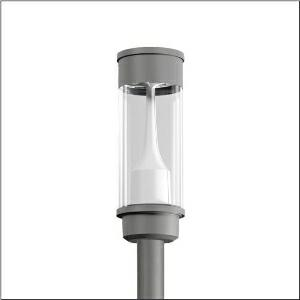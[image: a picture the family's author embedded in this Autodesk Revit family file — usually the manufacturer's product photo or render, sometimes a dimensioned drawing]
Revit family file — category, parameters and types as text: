
# Revit family: litepole_iq___p1_0a_5xa5415lf14h_d8b4
name_source: partatom
category: Lighting Fixtures
units: mm (PartAtom-declared; Revit-internal decimal feet)

## family parameters
Cut with Voids When Loaded = No
Host = Face
Light Source = No
Part Type = Normal
Room Calculation Point = No
Round Connector Dimension = Use Diameter
Shared = No

## types (1)
- --- (1 x LED, 1510 lm, 10 W, 4000K)
    Apparent Load = 10 VA
    CIE Flux Codes = 32 61 90 93 100
    Color Rendering = 70
    Color Temperature = 4000K
    Default Elevation = 1800 mm
    Description = Litepole iQ, mast luminaire, Module 540 iQ-SR, primary light control with 3 zone facetted reflector, of plastic, silver coated, highly specular, structured, primary optical cover: cover, of PMMA, transparent, partly coated, light distribution: P1.0a, light emission: direct distribution, primary light characteristic: strongly asymmetric, installation type: post-top, LED, High Power LED, rated luminous flux: 1.510lm, luminous efficacy: 151lm/W, light colour: 740, colour temperature: 4000K, control gear: iQ Street-Remote, control: optimised constant luminous flux control (CLO 2.0), Desk-Remote (wireless, voltage-free reading and setting of iQ features in the workshop via application-optimized NFC function/RFID function), Light-Fading, Smart-Wire, Night-Set, Lumen-Switch, Temp-Guard, Auto-Match, Street-Remote, pre-setting: logarithmic dimming characteristic, with terminal, 6-pole, max. 2.5mm², mains connection: 230..240V, AC, 50/60Hz, start of lifetime: 10W, end of service life: 10W, reduction: 5W, luminaire housing, upper part, of glass-fibre reinforced polyester, coated, Siteco® metallic grey (DB 702S), diameter: 210mm, height: 590mm, spigot size: d x l = 76 x 70mm (post-top) | with reducer (optional accessory) 60 x 70mm, mounting height: 3..5m, post-top mast mounting element, of diecast aluminium, coated, Siteco® metallic grey (DB 702S), Module 540 iQ-SR, traffic white (RAL 9016), equipment: standard, protection rating (complete): IP65, insulation class (complete): insulation class II (safety insulation), certification: CE, ENEC, VDE, packaging unit: 1 piece

Light Distribution: P1.0a
    Height = 590 mm
    Lamp = 1 x LED
    Lamp Light Flux = 1510 lm
    Lamp Power = 10 W
    Lamp count = 1
    Length = 220 mm
    Luminous efficacy = 151 lm/W
    Manufacturer = Siteco
    ModVariant = No
    Model = 5XA5415LF14H
    Number of Poles = 1
    OnlyDefault = Yes
    Power Factor = 1
    Product Name = Litepole iQ | P1.0a
    Product group = mast luminaire | pylon top
    ProductGroupID = 6100
    Protection Class = Protection class II
    Protection Degree = IP 65
    RLX_Detail_Level = 1
    RLX_Emergency_Light_Flux = 0 lm
    RLX_Emergency_Type = 0
    RLX_Emergency_Type_DB = No
    RlxData = <blob elided: 68441 chars, md5=58cc88a4>
    Socket = socket
    Standby Power = 0 W
    System Light Flux = 1510 lm
    System Power = 10 W
    Type Comments = factory setting: luminous flux: 100 % | dim-lin: 254 | 401 mA
    Type Image = l_1006025.jpg
    URL = http://relux.com
    VarID = @adj_180163
    Voltage = 0 V
    Weight = 0.00 kg
    Width = 0 mm  [stored 0 ft]

note: [stored X ft] marks values corroborated as IEEE doubles in the binary element streams (Revit-internal decimal feet)

## geometry (parser evidence)
native form markers: Blend x4, Sweep x11
no freeform markers — native parametric forms only
